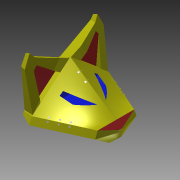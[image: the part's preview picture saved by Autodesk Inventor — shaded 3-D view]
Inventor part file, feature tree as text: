
AUTODESK INVENTOR PART (.ipt)
format: ipt  version: 2014 (Build 180170000, 170)  size: 540,160 bytes
history: native  units: in
note: dims shown in document units (in); Inventor stores cm internally (conversion verified against a paired STEP export)
features: sketch x17, extrude x11, plane x9, loft x4, projected_geometry x4, other x3, mirror x1
ambient origin geometry x8: Origin, YZ Plane, XZ Plane, XY Plane, X Axis, Y Axis, Z Axis, Center Point
bodies: Solid1 (feature_tree)
feature tree (49):
  sketch  "Sketch1"  dims[d0=0.7559in d1=0.7559in]
  plane  "Work Plane1"
  loft  "Loft1"
  extrude  "Extrusion1"  Depth=0.2in
  plane  "Work Plane4"
  loft  "Loft2"
  plane  "Work Plane5"
  loft  "Loft3"
  loft  "Loft4"
  extrude  "Extrusion2"  TaperAngle=0.0deg  [1 undecoded]
  plane  "Work Plane6"
  extrude  "Extrusion3"  Depth=1.0in
  extrude  "Extrusion4"  Depth=1.0651in
  extrude  "Extrusion5"  Depth=0.962in
  plane  "Work Plane7"
  extrude  "Extrusion6"  Depth=0.075in
  plane  "Work Plane8"
  other  "Work Axis1"
  plane  "Work Plane9"
  extrude  "Extrusion7"  Depth=0.06in
  mirror  "Mirror3"
  extrude  "Extrusion8"  Depth=0.05in
  plane  "Work Plane10"
  extrude  "Extrusion9"  Depth=0.0625in
  plane  "Work Plane11"
  extrude  "Extrusion10"  Depth=0.075in
  extrude  "Extrusion11"  TaperAngle=0.0deg  [1 undecoded]
  sketch  "Sketch2"  dims[d2=0.9963in d3=0.2in]
  sketch  "Sketch3"  dims[d4=0.5in d6=0.08in]
  sketch  "Sketch4"  dims[d7=0.55in d8=150.0deg]
  other  "Edges1"
  sketch  "Sketch5"  dims[d9=150.0deg d14=0.33in]
  projected_geometry  "Projected Loop1"
  other  "Edges2"
  sketch  "Sketch6"  dims[d15=0.66in d18=0.0in d19=90.0deg]
  sketch  "Sketch7"  dims[d20=0.0in d21=90.0deg d22=1.0in]
  sketch  "Sketch8"  dims[d26=1.0651in d28=1.0651in]
  sketch  "Sketch9"  dims[d29=0.0in d30=0.962in]
  sketch  "Sketch10"  dims[d31=0.962in d32=0.075in]
  sketch  "Sketch11"  dims[d33=0.15in d34=0.06in]
  sketch  "Sketch12"  dims[d35=0.1in d36=0.05in]
  sketch  "Sketch13"  dims[d37=0.45in d38=0.0in d39=0.0625in]
  projected_geometry  "Projected Loop2"
  projected_geometry  "Projected Loop3"
  sketch  "Sketch14"  dims[d40=0.01in d41=0.075in]
  projected_geometry  "Projected Loop4"
  sketch  "Sketch15"  dims[d42=0.01in d43=0.0in d44=90.0deg]
  sketch  "Sketch16"  dims[d45=0.0in d46=90.0deg]
  sketch  "Sketch17"  dims[d47=0.2in d48=0.07in d49=0.0in d50=90.0deg d51=0.0in d52=90.0deg d53=0.01in d54=0.01in d55=0.0344in d56=150.0deg d57=60.0deg d58=150.0deg d59=0.7in d60=0.05in d61=0.05in d62=0.05in d63=0.05in d64=0.05in d65=0.01in d66=0.0in d67=90.0deg d68=0.0in d69=90.0deg d70=0.1in d71=0.4in d72=0.15in d73=0.05in d74=0.0in d75=0.02in d77=0.15in d78=0.02in d79=0.1in d80=0.1in d81=0.1in d82=0.02in d83=0.15in d84=0.05in d85=0.0in d86=0.045in d87=0.0in d88=0.025in d89=0.0in d90=0.02in d91=0.02in d92=0.005in d93=0.0in d94=90.0deg d95=0.4466in d96=1.0in d97=0.0in d98=1.0in d99=0.0in d100=0.6528in d101=0.0in d102=0.0in d103=1.0in d104=0.0in d106=90.0deg d107=1.0in d108=0.0in]
note: 2 required parameter values undecoded (feature->parameter linkage not recoverable at this tier; creation-order binding heuristic only, values carry confidence <= 0.55)
